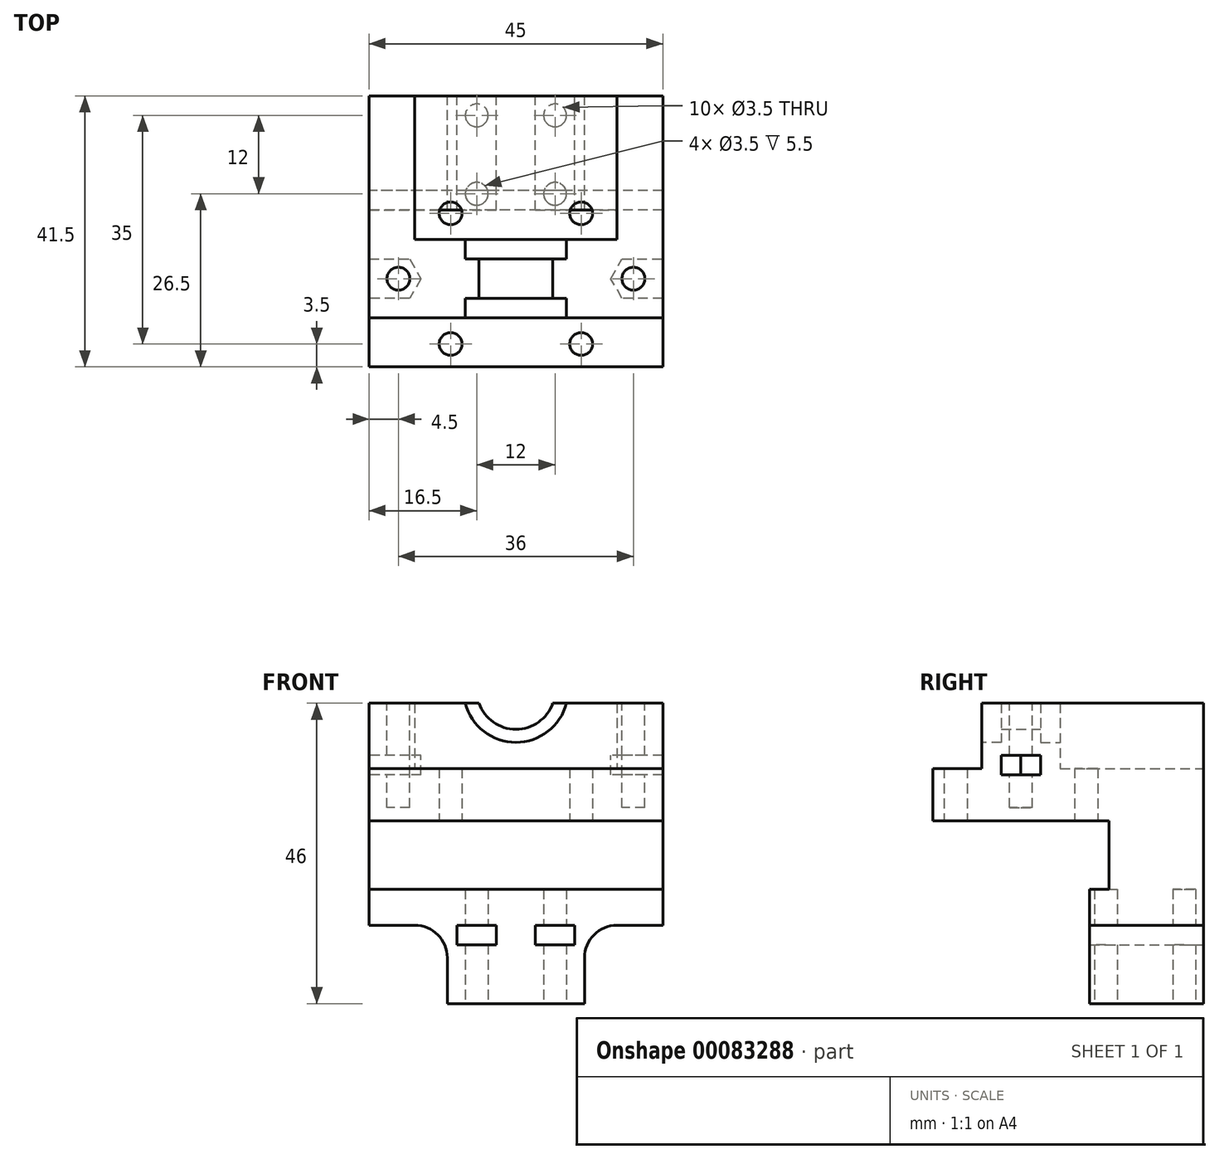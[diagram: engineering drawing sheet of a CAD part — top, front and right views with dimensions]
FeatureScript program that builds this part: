
annotation { "Feature Type Name" : "Feature", "Feature Type Description" : "" }
export const myFeature = defineFeature(function(context is Context, id is Id, definition is map)
    precondition{}
    {
        {
            var Q0;
            Q0=qCreatedBy(makeId("Top.planeOp"),FACE);
            var sketch = newSketch(context, id + "F0", { "sketchPlane" : qUnion([Q0])});
            skLineSegment(sketch, "E0.bottom", {"start": v(22.5, 13.5) * mm, "end": v(-22.5, 13.5) * mm});
            skLineSegment(sketch, "E0.top", {"start": v(22.5, -13.5) * mm, "end": v(-22.5, -13.5) * mm});
            skLineSegment(sketch, "E0.left", {"start": v(22.5, 13.5) * mm, "end": v(22.5, -13.5) * mm});
            skLineSegment(sketch, "E0.right", {"start": v(-22.5, 13.5) * mm, "end": v(-22.5, -13.5) * mm});
            skPoint(sketch, "E0.middle", {"position": v(0, 0) * mm});
            skLineSegment(sketch, "E1.bottom", {"start": v(10, 10) * mm, "end": v(-10, 10) * mm, "construction": true});
            skLineSegment(sketch, "E1.top", {"start": v(10, -10) * mm, "end": v(-10, -10) * mm, "construction": true});
            skLineSegment(sketch, "E1.left", {"start": v(10, 10) * mm, "end": v(10, -10) * mm, "construction": true});
            skLineSegment(sketch, "E1.right", {"start": v(-10, 10) * mm, "end": v(-10, -10) * mm, "construction": true});
            skCircle(sketch, "E2", {"center": v(10, 10) * mm, "radius": 1.75 * mm});
            skCircle(sketch, "E3", {"center": v(10, -10) * mm, "radius": 1.75 * mm});
            skCircle(sketch, "E4", {"center": v(-10, -10) * mm, "radius": 1.75 * mm});
            skCircle(sketch, "E5", {"center": v(-10, 10) * mm, "radius": 1.75 * mm});
            skLineSegment(sketch, "E6.top", {"start": v(22.5, 28) * mm, "end": v(-22.5, 28) * mm});
            skLineSegment(sketch, "E6.left", {"start": v(22.5, 13.5) * mm, "end": v(22.5, 28) * mm});
            skLineSegment(sketch, "E6.right", {"start": v(-22.5, 13.5) * mm, "end": v(-22.5, 28) * mm});
            skLineSegment(sketch, "E7", {"start": v(0, 0) * mm, "end": v(0, 35.1) * mm, "construction": true});
            skSolve(sketch);
        }
        {
            var Q0;
            Q0=makeQuery(id+"F0.imprint","IMPRINT",FACE,{"disambiguationData":[TD([[makeQuery(id+"F0.imprint","IMPRINT",EDGE,{"derivedFrom":sQuery(id+"F0.wireOp",EDGE,"E0.top")}),-1.0]])]});
            var Q1;
            Q1=makeQuery(id+"F0.imprint","IMPRINT",FACE,{"disambiguationData":[TD([[makeQuery(id+"F0.imprint","IMPRINT",EDGE,{"derivedFrom":sQuery(id+"F0.wireOp",EDGE,"E0.bottom")}),-1.0]])]});
            extrude(context, id + "F1", {"entities" : qUnion([Q0, Q1]), "depth" : 8 * mm});
        }
        {
            var Q0;
            Q0=makeQuery(id+"F0.imprint","IMPRINT",FACE,{"disambiguationData":[TD([[makeQuery(id+"F0.imprint","IMPRINT",EDGE,{"derivedFrom":sQuery(id+"F0.wireOp",EDGE,"E0.bottom")}),-1.0]])]});
            extrude(context, id + "F2", {"entities" : qUnion([Q0]), "operationType" : NewBodyOperationType.ADD, "oppositeDirection" : true, "depth" : 28 * mm});
        }
        {
            var Q0;
            Q0=makeQuery(id+"F1.opExtrude","CAP_FACE",FACE,{"disambiguationData":[OSD([sQuery(id+"F0.wireOp",EDGE,"E0.top"),sQuery(id+"F0.wireOp",EDGE,"E0.left"),sQuery(id+"F0.wireOp",EDGE,"E0.right"),sQuery(id+"F0.wireOp",EDGE,"E2"),sQuery(id+"F0.wireOp",EDGE,"E3"),sQuery(id+"F0.wireOp",EDGE,"E4"),sQuery(id+"F0.wireOp",EDGE,"E5"),sQuery(id+"F0.wireOp",EDGE,"E6.top"),sQuery(id+"F0.wireOp",EDGE,"E6.left"),sQuery(id+"F0.wireOp",EDGE,"E6.right"),sQuery(id+"F0.wireOp",EDGE,"wM1XhkJN-trMY-uXqw-IaT3-WCdx9zgbR3Wi"),sQuery(id+"F0.wireOp",EDGE,"QNUtfYZv-23Et-IRuA-WR7Z-BPJWFs7D9J4Z")])],"isStart":false});
            var sketch = newSketch(context, id + "F3", { "sketchPlane" : qUnion([Q0])});
            skLineSegment(sketch, "E8.bottom", {"start": v(-22.5, -6) * mm, "end": v(-15.5, -6) * mm});
            skLineSegment(sketch, "E8.top", {"start": v(-22.5, 28) * mm, "end": v(-15.5, 28) * mm});
            skLineSegment(sketch, "E8.left", {"start": v(-22.5, -6) * mm, "end": v(-22.5, 28) * mm});
            skLineSegment(sketch, "E8.right", {"start": v(-15.5, -6) * mm, "end": v(-15.5, 28) * mm});
            skLineSegment(sketch, "E9.bottom", {"start": v(22.5, -6) * mm, "end": v(15.5, -6) * mm});
            skLineSegment(sketch, "E9.top", {"start": v(22.5, 28) * mm, "end": v(15.5, 28) * mm});
            skLineSegment(sketch, "E9.left", {"start": v(22.5, -6) * mm, "end": v(22.5, 28) * mm});
            skLineSegment(sketch, "E9.right", {"start": v(15.5, -6) * mm, "end": v(15.5, 28) * mm});
            skLineSegment(sketch, "E10.bottom", {"start": v(-15.5, -6) * mm, "end": v(15.5, -6) * mm});
            skLineSegment(sketch, "E10.top", {"start": v(-15.5, 6) * mm, "end": v(15.5, 6) * mm});
            skLineSegment(sketch, "E10.left", {"start": v(-15.5, -6) * mm, "end": v(-15.5, 6) * mm});
            skLineSegment(sketch, "E10.right", {"start": v(15.5, -6) * mm, "end": v(15.5, 6) * mm});
            skSolve(sketch);
        }
        {
            var Q0;
            Q0=qSketchRegion(id+"F3",true);
            extrude(context, id + "F4", {"entities" : qUnion([Q0]), "operationType" : NewBodyOperationType.ADD, "depth" : 10 * mm});
        }
        {
            var Q0;
            Q0=makeQuery(id+"F4.opExtrude","SWEPT_FACE",FACE,{"disambiguationData":[OSD([sQuery(id+"F3.wireOp",EDGE,"E10.top")])]});
            var sketch = newSketch(context, id + "F5", { "sketchPlane" : qUnion([Q0])});
            skCircle(sketch, "E11", {"center": v(0, 20) * mm, "radius": 8 * mm});
            skCircle(sketch, "E12", {"center": v(0, 20) * mm, "radius": 6 * mm});
            skSolve(sketch);
        }
        {
            var Q0;
            {var subQ0=sQuery(id+"F5.wireOp",EDGE,"E12");var subQ1=makeQuery(id+"F4.opExtrude","CAP_EDGE",EDGE,{"disambiguationData":[OSD([sQuery(id+"F3.wireOp",EDGE,"E10.top")])],"isStart":false});var subQ2=makeQuery(id+"F5.imprint","INTERSECT",VERTEX,{"disambiguationData":[OD(0.0)],"derivedFrom":[subQ1,subQ0]});Q0=makeQuery(id+"F5.imprint","IMPRINT",FACE,{"disambiguationData":[TD([[makeQuery(id+"F5.imprint","IMPRINT",EDGE,{"disambiguationData":[TD([[subQ2,1.0]])],"derivedFrom":subQ0}),1.0]])]});}
            extrude(context, id + "F6", {"entities" : qUnion([Q0]), "operationType" : NewBodyOperationType.REMOVE, "endBound" : BoundingType.THROUGH_ALL, "oppositeDirection" : true, "depth" : 25 * mm});
        }
        {
            var Q0;
            {var subQ0=sQuery(id+"F5.wireOp",EDGE,"E11");var subQ1=makeQuery(id+"F4.opExtrude","CAP_EDGE",EDGE,{"disambiguationData":[OSD([sQuery(id+"F3.wireOp",EDGE,"E10.top")])],"isStart":false});var subQ2=makeQuery(id+"F5.imprint","INTERSECT",VERTEX,{"disambiguationData":[OD(0.0)],"derivedFrom":[subQ1,subQ0]});Q0=makeQuery(id+"F5.imprint","IMPRINT",FACE,{"disambiguationData":[TD([[makeQuery(id+"F5.imprint","IMPRINT",EDGE,{"disambiguationData":[TD([[subQ2,1.0]])],"derivedFrom":subQ0}),1.0]])]});}
            extrude(context, id + "F7", {"entities" : qUnion([Q0]), "operationType" : NewBodyOperationType.REMOVE, "oppositeDirection" : true, "depth" : 3 * mm});
        }
        {
            var Q0;
            Q0=makeQuery(id+"F4.opExtrude","SWEPT_FACE",FACE,{"disambiguationData":[OSD([sQuery(id+"F3.wireOp",EDGE,"E10.bottom")])]});
            var sketch = newSketch(context, id + "F8", { "sketchPlane" : qUnion([Q0])});
            skCircle(sketch, "E13", {"center": v(0, 20) * mm, "radius": 8 * mm});
            skSolve(sketch);
        }
        {
            var Q0;
            Q0=qSketchRegion(id+"F8",true);
            extrude(context, id + "F9", {"entities" : qUnion([Q0]), "operationType" : NewBodyOperationType.REMOVE, "oppositeDirection" : true, "depth" : 3 * mm});
        }
        {
            var Q0;
            {var subQ0=sQuery(id+"F0.wireOp",EDGE,"E6.right");var subQ1=sQuery(id+"F3.wireOp",EDGE,"E8.right");var subQ2=sQuery(id+"F3.wireOp",EDGE,"E8.bottom");var subQ4=sQuery(id+"F3.wireOp",EDGE,"E10.bottom");var subQ5=sQuery(id+"F3.wireOp",EDGE,"E8.left");var subQ6=sQuery(id+"F3.wireOp",EDGE,"E10.top");var subQ7=sQuery(id+"F3.wireOp",EDGE,"E8.top");Q0=makeQuery(id+"F6.boolean.opBoolean","SPLIT",FACE,{"disambiguationData":[TD([makeQuery(id+"F2.opExtrude","SWEPT_FACE",FACE,{"disambiguationData":[OSD([subQ0])]})])],"derivedFrom":makeQuery(id+"F4.opExtrude","CAP_FACE",FACE,{"disambiguationData":[OSD([subQ2,subQ7,subQ5,subQ1,sQuery(id+"F3.wireOp",EDGE,"E9.bottom"),sQuery(id+"F3.wireOp",EDGE,"E9.top"),sQuery(id+"F3.wireOp",EDGE,"E9.left"),sQuery(id+"F3.wireOp",EDGE,"E9.right"),subQ4,subQ6])],"isStart":false})});}
            var sketch = newSketch(context, id + "F10", { "sketchPlane" : qUnion([Q0])});
            skCircle(sketch, "E14.cCircle", {"center": v(-18, 0) * mm, "radius": 3 * mm, "construction": true});
            skLineSegment(sketch, "E14.0", {"start": v(-16.27, -3) * mm, "end": v(-19.73, -3) * mm});
            skLineSegment(sketch, "E14.3", {"start": v(-19.73, 3) * mm, "end": v(-16.27, 3) * mm});
            skLineSegment(sketch, "E14.4", {"start": v(-16.27, 3) * mm, "end": v(-14.54, 0) * mm});
            skLineSegment(sketch, "E14.5", {"start": v(-14.54, 0) * mm, "end": v(-16.27, -3) * mm});
            skPoint(sketch, "E14.0.midPoint", {"position": v(-18, -3) * mm});
            skCircle(sketch, "E15.cCircle", {"center": v(18, 0) * mm, "radius": 3 * mm, "construction": true});
            skLineSegment(sketch, "E15.0", {"start": v(16.27, -3) * mm, "end": v(14.54, 0) * mm});
            skLineSegment(sketch, "E15.1", {"start": v(14.54, 0) * mm, "end": v(16.27, 3) * mm});
            skLineSegment(sketch, "E15.2", {"start": v(16.27, 3) * mm, "end": v(19.34, 3) * mm});
            skLineSegment(sketch, "E15.5", {"start": v(19.73, -3) * mm, "end": v(16.27, -3) * mm});
            skPoint(sketch, "E15.0.midPoint", {"position": v(15.4, -1.5) * mm});
            skLineSegment(sketch, "E16", {"start": v(19.34, 3) * mm, "end": v(22.5, 3) * mm});
            skLineSegment(sketch, "E17", {"start": v(19.73, -3) * mm, "end": v(22.5, -3) * mm});
            skLineSegment(sketch, "E18", {"start": v(-19.73, -3) * mm, "end": v(-22.5, -3) * mm});
            skLineSegment(sketch, "E19", {"start": v(-19.73, 3) * mm, "end": v(-22.5, 3) * mm});
            skLineSegment(sketch, "E20", {"start": v(-22.5, -3) * mm, "end": v(-22.5, 3) * mm});
            skLineSegment(sketch, "E21", {"start": v(22.5, -3) * mm, "end": v(22.5, 3) * mm});
            skSolve(sketch);
        }
        {
            var Q0;
            Q0=qSketchRegion(id+"F10",true);
            extrude(context, id + "F11", {"entities" : qUnion([Q0]), "operationType" : NewBodyOperationType.REMOVE, "oppositeDirection" : true, "depth" : 11 * mm});
        }
        {
            var Q0;
            Q0=qSketchRegion(id+"F10",true);
            extrude(context, id + "F12", {"entities" : qUnion([Q0]), "operationType" : NewBodyOperationType.ADD, "oppositeDirection" : true, "depth" : 8 * mm});
        }
        {
            var Q0;
            Q0=makeQuery(id+"F10.imprint","IMPRINT",FACE,{"disambiguationData":[TD([[makeQuery(id+"F10.imprint","IMPRINT",EDGE,{"derivedFrom":sQuery(id+"F10.wireOp",EDGE,"E14.0")}),1.0]])]});
            var sketch = newSketch(context, id + "F13", { "sketchPlane" : qUnion([Q0])});
            skCircle(sketch, "E22", {"center": v(-18, 0) * mm, "radius": 1.75 * mm});
            skCircle(sketch, "E23", {"center": v(18, 0) * mm, "radius": 1.75 * mm});
            skSolve(sketch);
        }
        {
            var Q0;
            Q0=qSketchRegion(id+"F13",true);
            extrude(context, id + "F14", {"entities" : qUnion([Q0]), "operationType" : NewBodyOperationType.REMOVE, "oppositeDirection" : true, "depth" : 16 * mm});
        }
        {
            var Q0;
            {var subQ0=sQuery(id+"F0.wireOp",EDGE,"E6.top");var subQ1=makeQuery(id+"F2.opExtrude","CAP_EDGE",EDGE,{"disambiguationData":[OSD([subQ0])],"isStart":false});Q0=makeQuery(id+"F4.boolean.opBoolean","MERGE",FACE,{"derivedFrom":[makeQuery(id+"F7nm2xFxYodMML4_1.boolean.opBoolean","MERGE",FACE,{"derivedFrom":[makeQuery(id+"F2.boolean.opBoolean","MERGE",FACE,{"derivedFrom":[makeQuery(id+"F1.opExtrude","SWEPT_FACE",FACE,{"disambiguationData":[OSD([subQ0])]}),makeQuery(id+"F2.opExtrude","SWEPT_FACE",FACE,{"disambiguationData":[OSD([subQ0])]})]}),makeQuery(id+"F7nm2xFxYodMML4_1.opExtrude","SWEPT_FACE",FACE,{"disambiguationData":[OSD([subQ0]),TDD([makeQuery(id+"Fbmr6vA98BlIakt_1.imprint","IMPRINT",EDGE,{"disambiguationData":[TD([[makeQuery(id+"Fbmr6vA98BlIakt_1.imprint","INTERSECT",VERTEX,{"derivedFrom":[subQ1,sQuery(id+"Fbmr6vA98BlIakt_1.wireOp",EDGE,"svRpLjLB-O1rV-L0s8-6DIm-nDr5cEQW5kL5")]}),-1.0]])],"derivedFrom":subQ1})])]}),makeQuery(id+"F7nm2xFxYodMML4_1.opExtrude","SWEPT_FACE",FACE,{"disambiguationData":[OSD([subQ0]),TDD([makeQuery(id+"Fbmr6vA98BlIakt_1.imprint","IMPRINT",EDGE,{"disambiguationData":[TD([[makeQuery(id+"Fbmr6vA98BlIakt_1.imprint","INTERSECT",VERTEX,{"derivedFrom":[subQ1,sQuery(id+"Fbmr6vA98BlIakt_1.wireOp",EDGE,"PJuHDjbe-c5Ev-mOzx-rbrg-ZDcgbhiueFlQ")]}),1.0]])],"derivedFrom":subQ1})])]})]}),makeQuery(id+"F4.opExtrude","SWEPT_FACE",FACE,{"disambiguationData":[OSD([sQuery(id+"F3.wireOp",EDGE,"E8.top")])]}),makeQuery(id+"F4.opExtrude","SWEPT_FACE",FACE,{"disambiguationData":[OSD([sQuery(id+"F3.wireOp",EDGE,"E9.top")])]})]});}
            var sketch = newSketch(context, id + "F15", { "sketchPlane" : qUnion([Q0])});
            skLineSegment(sketch, "E24.bottom", {"start": v(-22.5, -28) * mm, "end": v(-10.5, -28) * mm});
            skLineSegment(sketch, "E24.top", {"start": v(-22.5, -16) * mm, "end": v(-10.5, -16) * mm});
            skLineSegment(sketch, "E24.left", {"start": v(-22.5, -28) * mm, "end": v(-22.5, -16) * mm});
            skLineSegment(sketch, "E24.right", {"start": v(-10.5, -28) * mm, "end": v(-10.5, -16) * mm});
            skLineSegment(sketch, "E25.bottom", {"start": v(22.5, -28) * mm, "end": v(10.5, -28) * mm});
            skLineSegment(sketch, "E25.top", {"start": v(22.5, -16) * mm, "end": v(10.5, -16) * mm});
            skLineSegment(sketch, "E25.left", {"start": v(22.5, -28) * mm, "end": v(22.5, -16) * mm});
            skLineSegment(sketch, "E25.right", {"start": v(10.5, -28) * mm, "end": v(10.5, -16) * mm});
            skLineSegment(sketch, "E26.bottom", {"start": v(-22.5, -10.5) * mm, "end": v(22.5, -10.5) * mm});
            skLineSegment(sketch, "E26.top", {"start": v(-22.5, -28) * mm, "end": v(22.5, -28) * mm});
            skLineSegment(sketch, "E26.left", {"start": v(-22.5, -10.5) * mm, "end": v(-22.5, -28) * mm});
            skLineSegment(sketch, "E26.right", {"start": v(22.5, -10.5) * mm, "end": v(22.5, -28) * mm});
            skSolve(sketch);
        }
        {
            var Q0;
            {var subQ0=sQuery(id+"F15.wireOp",EDGE,"E25.top");Q0=makeQuery(id+"F15.imprint","IMPRINT",FACE,{"disambiguationData":[TD([[makeQuery(id+"F15.imprint","IMPRINT",EDGE,{"derivedFrom":subQ0}),1.0]])]});}
            var Q1;
            {var subQ0=sQuery(id+"F15.wireOp",EDGE,"E24.top");Q1=makeQuery(id+"F15.imprint","IMPRINT",FACE,{"disambiguationData":[TD([[makeQuery(id+"F15.imprint","IMPRINT",EDGE,{"derivedFrom":subQ0}),-1.0]])]});}
            extrude(context, id + "F16", {"entities" : qUnion([Q0, Q1]), "operationType" : NewBodyOperationType.REMOVE, "endBound" : BoundingType.THROUGH_ALL, "oppositeDirection" : true, "depth" : 25 * mm});
        }
        {
            var Q0;
            {var subQ3=sQuery(id+"F15.wireOp",EDGE,"E24.top");Q0=makeQuery(id+"F15.imprint","IMPRINT",FACE,{"disambiguationData":[TD([[makeQuery(id+"F15.imprint","IMPRINT",EDGE,{"derivedFrom":subQ3}),1.0]])]});}
            extrude(context, id + "F17", {"entities" : qUnion([Q0]), "operationType" : NewBodyOperationType.ADD, "oppositeDirection" : true, "depth" : 17.5 * mm});
        }
        {
            var Q0;
            Q0=makeQuery(id+"F17.boolean.opBoolean","MERGE",FACE,{"derivedFrom":[makeQuery(id+"F2.opExtrude","CAP_FACE",FACE,{"disambiguationData":[OSD([sQuery(id+"F0.wireOp",EDGE,"E0.bottom"),sQuery(id+"F0.wireOp",EDGE,"E6.top"),sQuery(id+"F0.wireOp",EDGE,"E6.left"),sQuery(id+"F0.wireOp",EDGE,"E6.right")])],"isStart":false}),makeQuery(id+"F17.opExtrude","SWEPT_FACE",FACE,{"disambiguationData":[OSD([sQuery(id+"F15.wireOp",EDGE,"E26.top")])]})]});
            var sketch = newSketch(context, id + "F18", { "sketchPlane" : qUnion([Q0])});
            skLineSegment(sketch, "E27.bottom", {"start": v(-6, -25) * mm, "end": v(6, -25) * mm, "construction": true});
            skLineSegment(sketch, "E27.top", {"start": v(-6, -13) * mm, "end": v(6, -13) * mm, "construction": true});
            skLineSegment(sketch, "E27.left", {"start": v(-6, -25) * mm, "end": v(-6, -13) * mm, "construction": true});
            skLineSegment(sketch, "E27.right", {"start": v(6, -25) * mm, "end": v(6, -13) * mm, "construction": true});
            skCircle(sketch, "E28", {"center": v(-6, -13) * mm, "radius": 1.75 * mm});
            skCircle(sketch, "E29", {"center": v(6, -13) * mm, "radius": 1.75 * mm});
            skCircle(sketch, "E30", {"center": v(6, -25) * mm, "radius": 1.75 * mm});
            skCircle(sketch, "E31", {"center": v(-6, -25) * mm, "radius": 1.75 * mm});
            skSolve(sketch);
        }
        {
            var Q0;
            Q0 = qSketchRegion(id + "F18", true);
            extrude(context, id + "F19", {"entities" : qUnion([Q0]), "operationType" : NewBodyOperationType.REMOVE, "oppositeDirection" : true, "depth" : 17.5 * mm});
        }
        {
            var Q0;
            {var subQ3=sQuery(id+"F15.wireOp",EDGE,"E24.top");Q0=makeQuery(id+"F15.imprint","IMPRINT",FACE,{"disambiguationData":[TD([[makeQuery(id+"F15.imprint","IMPRINT",EDGE,{"derivedFrom":subQ3}),1.0]])]});}
            var sketch = newSketch(context, id + "F20", { "sketchPlane" : qUnion([Q0])});
            skLineSegment(sketch, "E32.bottom", {"start": v(-3, -16) * mm, "end": v(-9, -16) * mm});
            skLineSegment(sketch, "E32.top", {"start": v(-3, -19) * mm, "end": v(-9, -19) * mm});
            skLineSegment(sketch, "E32.left", {"start": v(-3, -16) * mm, "end": v(-3, -19) * mm});
            skLineSegment(sketch, "E32.right", {"start": v(-9, -16) * mm, "end": v(-9, -19) * mm});
            skPoint(sketch, "E32.middle", {"position": v(-6, -17.5) * mm});
            skLineSegment(sketch, "E33.bottom", {"start": v(9, -16) * mm, "end": v(3, -16) * mm});
            skLineSegment(sketch, "E33.top", {"start": v(9, -19) * mm, "end": v(3, -19) * mm});
            skLineSegment(sketch, "E33.left", {"start": v(9, -16) * mm, "end": v(9, -19) * mm});
            skLineSegment(sketch, "E33.right", {"start": v(3, -16) * mm, "end": v(3, -19) * mm});
            skPoint(sketch, "E33.middle", {"position": v(6, -17.5) * mm});
            skSolve(sketch);
        }
        {
            var Q0;
            Q0 = qSketchRegion(id + "F20", true);
            extrude(context, id + "F21", {"entities" : qUnion([Q0]), "operationType" : NewBodyOperationType.REMOVE, "endBound" : BoundingType.THROUGH_ALL, "oppositeDirection" : true, "depth" : 25 * mm});
        }
        {
            var Q0;
            {var subQ0=sQuery(id+"F15.wireOp",EDGE,"E25.right");var subQ1=sQuery(id+"F15.wireOp",EDGE,"E25.top");Q0=makeQuery(id+"F17.boolean.opBoolean","MERGE",EDGE,{"derivedFrom":[makeQuery(id+"F16.boolean.opBoolean","COPY",EDGE,{"derivedFrom":makeQuery(id+"F16.opExtrude","SWEPT_EDGE",EDGE,{"disambiguationData":[OSD([subQ1,subQ0])]})}),makeQuery(id+"F17.opExtrude","SWEPT_EDGE",EDGE,{"disambiguationData":[OSD([subQ1,subQ0])]})]});}
            var Q1;
            {var subQ0=sQuery(id+"F15.wireOp",EDGE,"E24.right");var subQ1=sQuery(id+"F15.wireOp",EDGE,"E24.top");Q1=makeQuery(id+"F17.boolean.opBoolean","MERGE",EDGE,{"derivedFrom":[makeQuery(id+"F16.boolean.opBoolean","COPY",EDGE,{"derivedFrom":makeQuery(id+"F16.opExtrude","SWEPT_EDGE",EDGE,{"disambiguationData":[OSD([subQ1,subQ0])]})}),makeQuery(id+"F17.opExtrude","SWEPT_EDGE",EDGE,{"disambiguationData":[OSD([subQ1,subQ0])]})]});}
            fillet(context, id + "F22", {"entities" : qUnion([Q0, Q1]), "radius" : 5 * mm, "tangentPropagation" : true, "allowEdgeOverflow" : false});
        }
    });
